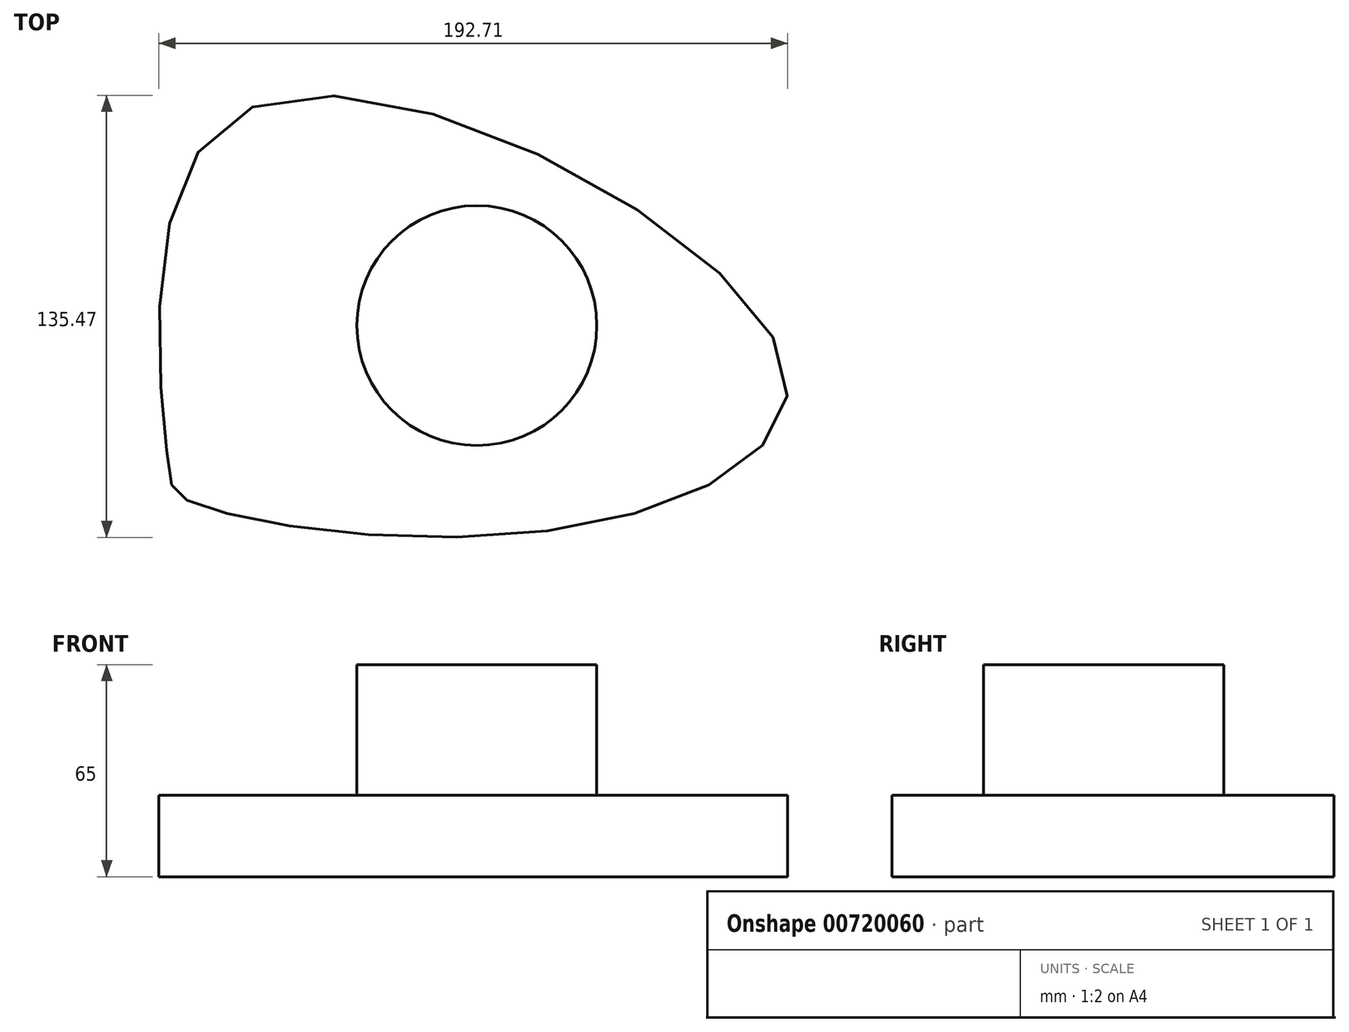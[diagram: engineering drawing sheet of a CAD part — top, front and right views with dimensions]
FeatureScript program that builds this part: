
annotation { "Feature Type Name" : "Feature", "Feature Type Description" : "" }
export const myFeature = defineFeature(function(context is Context, id is Id, definition is map)
    precondition{}
    {
        {
            var Q0;
            Q0=qCreatedBy(makeId("Top.planeOp"),FACE);
            var sketch = newSketch(context, id + "F0", { "sketchPlane" : qUnion([Q0])});
            skFitSpline(sketch, "E0", {"points": [v(-110.25, -23.62) * mm, v(-116.07, -11.78) * mm, v(-94.17, 95.1) * mm, v(72.33, 19.97) * mm, v(6.65, -32.14) * mm, v(-110.25, -23.62) * mm]});
            skSolve(sketch);
        }
        {
            var Q0;
            Q0=makeQuery(id+"F0.imprint","IMPRINT",FACE,{"disambiguationData":[TD([[makeQuery(id+"F0.imprint","IMPRINT",EDGE,{"derivedFrom":sQuery(id+"F0.wireOp",EDGE,"E0")}),-1.0]])]});
            extrude(context, id + "F1", {"entities" : qUnion([Q0]), "depth" : 25 * mm, "offsetDistance" : 25 * mm});
        }
        {
            var Q0;
            Q0=makeQuery(id+"F1.opExtrude","CAP_FACE",FACE,{"disambiguationData":[OSD([sQuery(id+"F0.wireOp",EDGE,"E0")])],"isStart":false});
            var sketch = newSketch(context, id + "F2", { "sketchPlane" : qUnion([Q0])});
            skCircle(sketch, "E1", {"center": v(-21.36, 29.93) * mm, "radius": 36.77 * mm});
            skSolve(sketch);
        }
        {
            var Q0;
            Q0=makeQuery(id+"F2.imprint","IMPRINT",FACE,{"disambiguationData":[TD([[makeQuery(id+"F2.imprint","IMPRINT",EDGE,{"derivedFrom":sQuery(id+"F2.wireOp",EDGE,"E1")}),1.0]])]});
            extrude(context, id + "F3", {"entities" : qUnion([Q0]), "operationType" : NewBodyOperationType.ADD, "depth" : 40 * mm, "offsetDistance" : 25 * mm});
        }
    });
